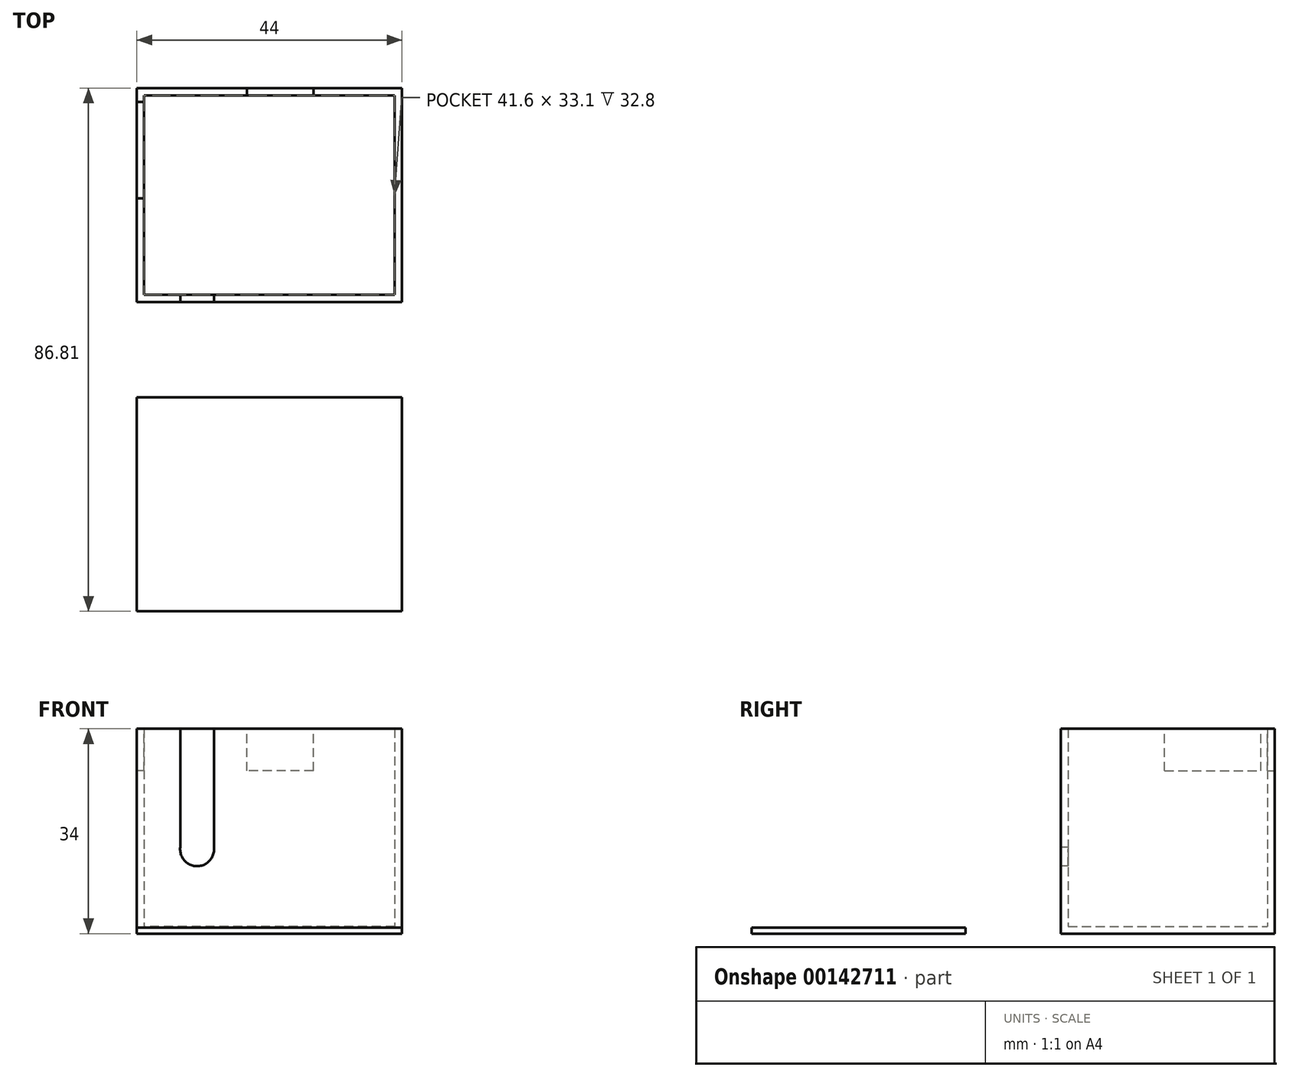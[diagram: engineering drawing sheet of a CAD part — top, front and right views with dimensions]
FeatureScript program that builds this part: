
annotation { "Feature Type Name" : "Feature", "Feature Type Description" : "" }
export const myFeature = defineFeature(function(context is Context, id is Id, definition is map)
    precondition{}
    {
        {
            var Q0;
            Q0=qCreatedBy(makeId("Top.planeOp"),FACE);
            var sketch = newSketch(context, id + "F0", { "sketchPlane" : qUnion([Q0])});
            skLineSegment(sketch, "E0.bottom", {"start": v(22, -17.75) * mm, "end": v(-22, -17.75) * mm});
            skLineSegment(sketch, "E0.top", {"start": v(22, 17.75) * mm, "end": v(-22, 17.75) * mm});
            skLineSegment(sketch, "E0.left", {"start": v(22, -17.75) * mm, "end": v(22, 17.75) * mm});
            skLineSegment(sketch, "E0.right", {"start": v(-22, -17.75) * mm, "end": v(-22, 17.75) * mm});
            skPoint(sketch, "E0.middle", {"position": v(0, 0) * mm});
            skSolve(sketch);
        }
        {
            var Q0;
            Q0 = qSketchRegion(id + "F0", true);
            extrude(context, id + "F1", {"entities" : qUnion([Q0]), "depth" : 34 * mm});
        }
        {
            var Q0;
            Q0=makeQuery(id+"F1.opExtrude","CAP_FACE",FACE,{"disambiguationData":[OSD([sQuery(id+"F0.wireOp",EDGE,"E0.bottom"),sQuery(id+"F0.wireOp",EDGE,"E0.top"),sQuery(id+"F0.wireOp",EDGE,"E0.left"),sQuery(id+"F0.wireOp",EDGE,"E0.right")])],"isStart":false});
            shell(context, id + "F2", {"entities" : qUnion([Q0]), "thickness" : 1.2 * mm});
        }
        {
            var Q0;
            Q0=makeQuery(id+"F1.opExtrude","SWEPT_FACE",FACE,{"disambiguationData":[OSD([sQuery(id+"F0.wireOp",EDGE,"E0.bottom")])]});
            var sketch = newSketch(context, id + "F3", { "sketchPlane" : qUnion([Q0])});
            skCircle(sketch, "E1", {"center": v(-12, 14) * mm, "radius": 2.81 * mm});
            skLineSegment(sketch, "E2.bottom", {"start": v(-9.19, 14) * mm, "end": v(-14.8, 14) * mm});
            skLineSegment(sketch, "E2.top", {"start": v(-9.19, 34) * mm, "end": v(-14.8, 34) * mm});
            skLineSegment(sketch, "E2.left", {"start": v(-9.19, 14) * mm, "end": v(-9.19, 34) * mm});
            skLineSegment(sketch, "E2.right", {"start": v(-14.8, 14) * mm, "end": v(-14.8, 34) * mm});
            skSolve(sketch);
        }
        {
            var Q0;
            Q0 = qSketchRegion(id + "F3", true);
            extrude(context, id + "F4", {"entities" : qUnion([Q0]), "operationType" : NewBodyOperationType.REMOVE, "endBound" : BoundingType.UP_TO_NEXT, "oppositeDirection" : true, "depth" : 25 * mm});
        }
        {
            var Q0;
            Q0=makeQuery(id+"F1.opExtrude","CAP_FACE",FACE,{"disambiguationData":[OSD([sQuery(id+"F0.wireOp",EDGE,"E0.bottom"),sQuery(id+"F0.wireOp",EDGE,"E0.top"),sQuery(id+"F0.wireOp",EDGE,"E0.left"),sQuery(id+"F0.wireOp",EDGE,"E0.right")])],"isStart":false});
            var sketch = newSketch(context, id + "F5", { "sketchPlane" : qUnion([Q0])});
            skLineSegment(sketch, "E3.bottom", {"start": v(7.3, 16.55) * mm, "end": v(-3.7, 16.55) * mm});
            skLineSegment(sketch, "E3.top", {"start": v(7.3, 17.75) * mm, "end": v(-3.7, 17.75) * mm});
            skLineSegment(sketch, "E3.left", {"start": v(7.3, 16.55) * mm, "end": v(7.3, 17.75) * mm});
            skLineSegment(sketch, "E3.right", {"start": v(-3.7, 16.55) * mm, "end": v(-3.7, 17.75) * mm});
            skLineSegment(sketch, "E4.bottom", {"start": v(-20.8, 15.45) * mm, "end": v(-22, 15.45) * mm});
            skLineSegment(sketch, "E4.top", {"start": v(-20.8, -0.55) * mm, "end": v(-22, -0.55) * mm});
            skLineSegment(sketch, "E4.left", {"start": v(-20.8, 15.45) * mm, "end": v(-20.8, -0.55) * mm});
            skLineSegment(sketch, "E4.right", {"start": v(-22, 15.45) * mm, "end": v(-22, -0.55) * mm});
            skSolve(sketch);
        }
        {
            var Q0;
            Q0 = qSketchRegion(id + "F5", true);
            extrude(context, id + "F6", {"entities" : qUnion([Q0]), "operationType" : NewBodyOperationType.REMOVE, "oppositeDirection" : true, "depth" : 7 * mm});
        }
        {
            var Q0;
            Q0=qCreatedBy(makeId("Top.planeOp"),FACE);
            var sketch = newSketch(context, id + "F7", { "sketchPlane" : qUnion([Q0])});
            skLineSegment(sketch, "E5.bottom", {"start": v(-22, -33.56) * mm, "end": v(22, -33.56) * mm});
            skLineSegment(sketch, "E5.top", {"start": v(-22, -69.06) * mm, "end": v(22, -69.06) * mm});
            skLineSegment(sketch, "E5.left", {"start": v(-22, -33.56) * mm, "end": v(-22, -69.06) * mm});
            skLineSegment(sketch, "E5.right", {"start": v(22, -33.56) * mm, "end": v(22, -69.06) * mm});
            skPoint(sketch, "E5.middle", {"position": v(0, -51.31) * mm});
            skSolve(sketch);
        }
        {
            var Q0;
            Q0 = qSketchRegion(id + "F7", true);
            extrude(context, id + "F8", {"entities" : qUnion([Q0]), "depth" : 1 * mm});
        }
    });
